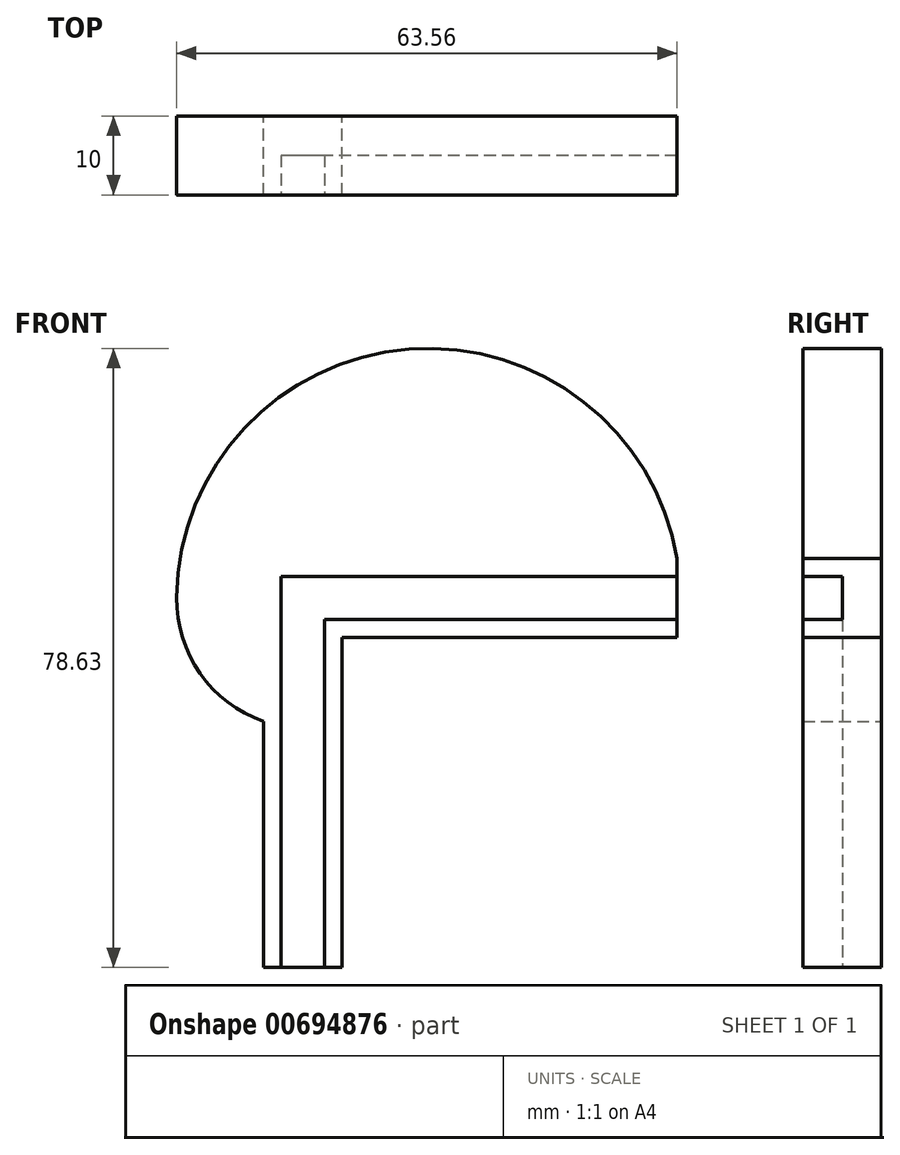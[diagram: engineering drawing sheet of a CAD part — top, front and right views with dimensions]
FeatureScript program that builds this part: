
annotation { "Feature Type Name" : "Feature", "Feature Type Description" : "" }
export const myFeature = defineFeature(function(context is Context, id is Id, definition is map)
    precondition{}
    {
        {
            var Q0;
            Q0=qCreatedBy(makeId("Front.planeOp"),FACE);
            var sketch = newSketch(context, id + "F0", { "sketchPlane" : qUnion([Q0])});
            skLineSegment(sketch, "E0.top", {"start": v(47.06, -4.88) * mm, "end": v(4.54, -4.88) * mm});
            skLineSegment(sketch, "E0.left", {"start": v(47.06, 5.12) * mm, "end": v(47.06, -4.88) * mm});
            skPoint(sketch, "E0.middle", {"position": v(18.18, 0.12) * mm});
            skLineSegment(sketch, "E1.bottom", {"start": v(4.54, -46.81) * mm, "end": v(-5.46, -46.81) * mm});
            skLineSegment(sketch, "E1.left", {"start": v(4.54, -46.81) * mm, "end": v(4.54, -4.88) * mm});
            skLineSegment(sketch, "E1.right", {"start": v(-5.46, -46.81) * mm, "end": v(-5.46, -15.57) * mm});
            skPoint(sketch, "E1.middle", {"position": v(-0.46, -17.76) * mm});
            skPoint(sketch, "E1.top.end.orphan", {"position": v(-5.46, 11.3) * mm});
            skPoint(sketch, "E2.orphan", {"position": v(4.54, 11.3) * mm});
            skPoint(sketch, "E0.right.end.orphan", {"position": v(-10.7, -4.88) * mm});
            skPoint(sketch, "E3.orphan", {"position": v(-10.7, 5.12) * mm});
            skPoint(sketch, "E4.top.end.orphan", {"position": v(2.58, 10.5) * mm});
            skPoint(sketch, "E4.top.start.orphan", {"position": v(-3.42, 10.5) * mm});
            skPoint(sketch, "E5.right.end.orphan", {"position": v(-10.5, 3.12) * mm});
            skPoint(sketch, "E6.orphan", {"position": v(-10.5, -2.88) * mm});
            skArc(sketch, "E7", {"start": v(-16.5, 0.19) * mm, "mid": v(-13.51, -9.47) * mm, "end": v(-5.46, -15.57) * mm});
            skArc(sketch, "E8", {"start": v(-16.5, 0.19) * mm, "mid": v(13.02, 31.73) * mm, "end": v(47.06, 5.12) * mm});
            skSolve(sketch);
        }
        {
            var Q0;
            Q0=makeQuery(id+"F0.imprint","IMPRINT",FACE,{"disambiguationData":[TD([[makeQuery(id+"F0.imprint","IMPRINT",EDGE,{"derivedFrom":sQuery(id+"F0.wireOp",EDGE,"e8d21304-5a39-48f1-8851-f26ec5e953e21")}),1.0]])]});
            var Q1;
            {var subQ4=sQuery(id+"F0.wireOp",EDGE,"E0.top");Q1=makeQuery(id+"F0.imprint","IMPRINT",FACE,{"disambiguationData":[TD([[makeQuery(id+"F0.imprint","IMPRINT",EDGE,{"derivedFrom":subQ4}),-1.0]])]});}
            var Q2;
            Q2=makeQuery(id+"F0.imprint","IMPRINT",FACE,{"disambiguationData":[TD([[makeQuery(id+"F0.imprint","IMPRINT",EDGE,{"derivedFrom":sQuery(id+"F0.wireOp",EDGE,"E5.bottom")}),-1.0]])]});
            extrude(context, id + "F1", {"entities" : qUnion([Q0, Q1, Q2]), "depth" : 10 * mm, "offsetDistance" : 25 * mm});
        }
        {
            var Q0;
            Q0=makeQuery(id+"F1.opExtrude","CAP_FACE",FACE,{"disambiguationData":[OSD([sQuery(id+"F0.wireOp",EDGE,"e8d21304-5a39-48f1-8851-f26ec5e953e21"),sQuery(id+"F0.wireOp",EDGE,"E0.bottom"),sQuery(id+"F0.wireOp",EDGE,"E0.top"),sQuery(id+"F0.wireOp",EDGE,"E0.left"),sQuery(id+"F0.wireOp",EDGE,"E1.bottom"),sQuery(id+"F0.wireOp",EDGE,"E1.left"),sQuery(id+"F0.wireOp",EDGE,"E1.right"),sQuery(id+"F0.wireOp",EDGE,"E5.left"),sQuery(id+"F0.wireOp",EDGE,"E4.bottom")])],"isStart":false});
            var sketch = newSketch(context, id + "F2", { "sketchPlane" : qUnion([Q0])});
            skLineSegment(sketch, "E9.bottom", {"start": v(47.06, 2.87) * mm, "end": v(-3.2, 2.87) * mm});
            skLineSegment(sketch, "E9.top", {"start": v(47.06, -2.63) * mm, "end": v(2.3, -2.63) * mm});
            skLineSegment(sketch, "E9.left", {"start": v(47.06, 2.87) * mm, "end": v(47.06, -2.63) * mm});
            skLineSegment(sketch, "E9.right", {"start": v(-3.2, 2.87) * mm, "end": v(-3.2, -2.63) * mm});
            skLineSegment(sketch, "E10.bottom", {"start": v(-3.2, -46.81) * mm, "end": v(2.3, -46.81) * mm});
            skLineSegment(sketch, "E10.left", {"start": v(-3.2, -46.81) * mm, "end": v(-3.2, -2.63) * mm});
            skLineSegment(sketch, "E10.right", {"start": v(2.3, -46.81) * mm, "end": v(2.3, -2.63) * mm});
            skLineSegment(sketch, "E11.trimOffspring", {"start": v(-3.2, -2.63) * mm, "end": v(-3.2, -2.63) * mm});
            skSolve(sketch);
        }
        {
            var Q0;
            Q0 = qSketchRegion(id + "F2", true);
            extrude(context, id + "F3", {"entities" : qUnion([Q0]), "operationType" : NewBodyOperationType.REMOVE, "oppositeDirection" : true, "depth" : 5 * mm, "offsetDistance" : 25 * mm});
        }
    });
